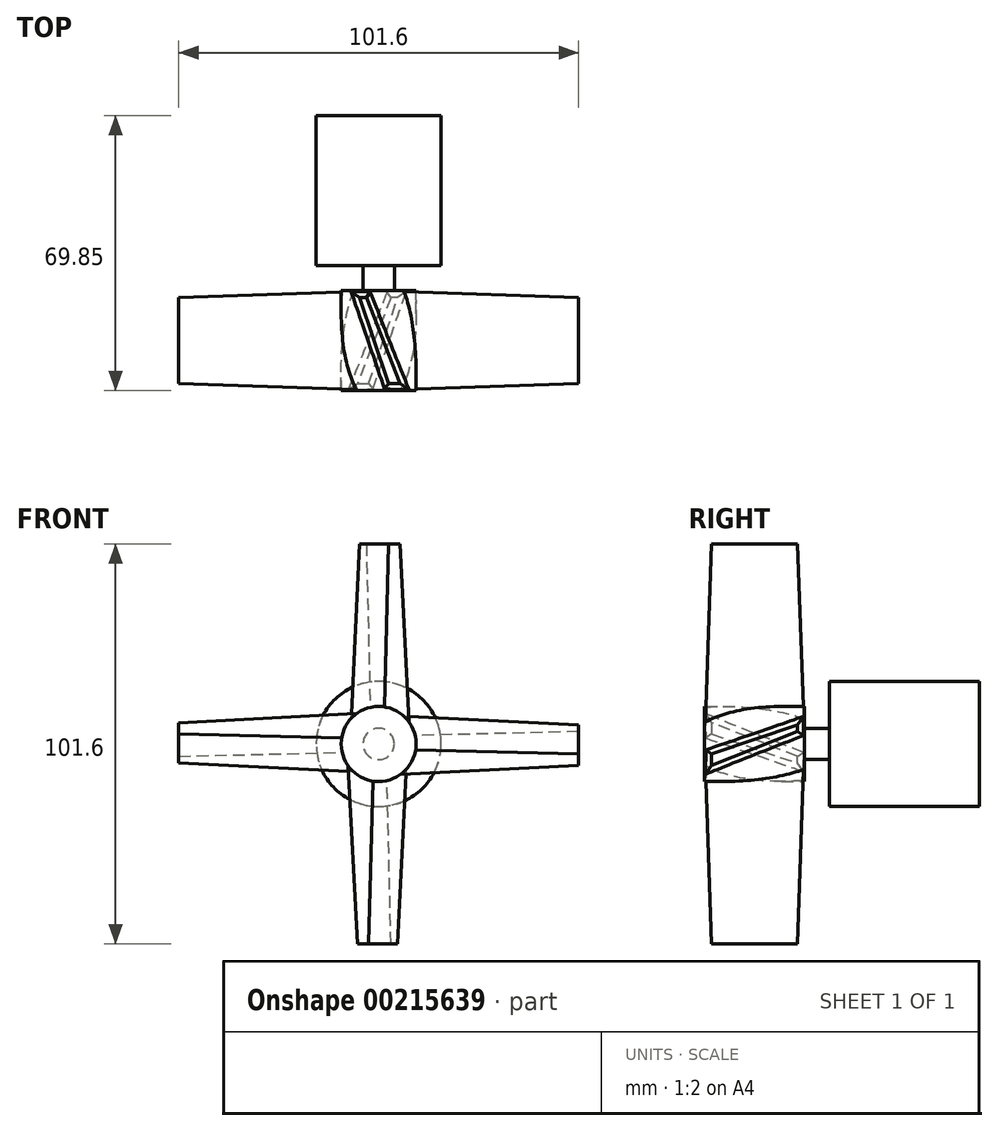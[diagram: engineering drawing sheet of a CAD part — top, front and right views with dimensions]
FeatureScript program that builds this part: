
annotation { "Feature Type Name" : "Feature", "Feature Type Description" : "" }
export const myFeature = defineFeature(function(context is Context, id is Id, definition is map)
    precondition{}
    {
        {
            var Q0;
            Q0=qCreatedBy(makeId("Front.planeOp"),FACE);
            var sketch = newSketch(context, id + "F0", { "sketchPlane" : qUnion([Q0])});
            skCircle(sketch, "E0", {"center": v(0, 0) * mm, "radius": 9.53 * mm});
            skSolve(sketch);
        }
        {
            var Q0;
            Q0=makeQuery(id+"F0.imprint","IMPRINT",FACE,{"disambiguationData":[TD([[makeQuery(id+"F0.imprint","IMPRINT",EDGE,{"derivedFrom":sQuery(id+"F0.wireOp",EDGE,"E0")}),1.0]])]});
            extrude(context, id + "F1", {"entities" : qUnion([Q0]), "depth" : 25.4 * mm});
        }
        {
            var Q0;
            Q0=qCreatedBy(makeId("Right.planeOp"),FACE);
            var sketch = newSketch(context, id + "F2", { "sketchPlane" : qUnion([Q0])});
            skLineSegment(sketch, "E1", {"start": v(0, 4.62) * mm, "end": v(-25.4, -4.62) * mm, "construction": true});
            skLineSegment(sketch, "E2", {"start": v(-12.7, 0) * mm, "end": v(0, 0) * mm, "construction": true});
            skPoint(sketch, "E3.orphan", {"position": v(-25.4, 0) * mm});
            skLineSegment(sketch, "E4", {"start": v(-12.7, 0) * mm, "end": v(-25.4, 0) * mm, "construction": true});
            skLineSegment(sketch, "E5", {"start": v(0, 7.33) * mm, "end": v(-25.4, -1.24) * mm});
            skLineSegment(sketch, "E6", {"start": v(0, 1.92) * mm, "end": v(-25.4, -8) * mm});
            skLineSegment(sketch, "E7", {"start": v(-25.4, -1.24) * mm, "end": v(-25.4, -8) * mm});
            skLineSegment(sketch, "E8", {"start": v(0, 7.33) * mm, "end": v(0, 1.92) * mm});
            skSolve(sketch);
        }
        {
            var Q0;
            Q0 = qSketchRegion(id + "F2", true);
            extrude(context, id + "F3", {"entities" : qUnion([Q0]), "depth" : 50.8 * mm, "hasDraft" : true, "draftAngle" : 2 * degree, "draftPullDirection" : true});
        }
        {
            var Q0;
            Q0=qCreatedBy(makeId("Right.planeOp"),FACE);
            var sketch = newSketch(context, id + "F4", { "sketchPlane" : qUnion([Q0])});
            skLineSegment(sketch, "E9", {"start": v(-25.4, 0) * mm, "end": v(0, 0) * mm});
            skSolve(sketch);
        }
        {
            var Q0;
            Q0=makeQuery(id+"F3.opExtrude","SWEPT_BODY",BODY,{"disambiguationData":[OSD([sQuery(id+"F2.wireOp",EDGE,"E5"),sQuery(id+"F2.wireOp",EDGE,"E6"),sQuery(id+"F2.wireOp",EDGE,"E7"),sQuery(id+"F2.wireOp",EDGE,"E8")])]});
            var Q1;
            Q1=sQuery(id+"F4.wireOp",EDGE,"E9");
            circularPattern(context, id + "F5", {"operationType" : NewBodyOperationType.ADD, "entities" : qUnion([Q0]), "axis" : qUnion([Q1]), "angle" : 360 * degree, "instanceCount" : 4, "equalSpace" : true});
        }
        {
            var Q0;
            Q0=makeQuery(id+"F1.opExtrude","CAP_FACE",FACE,{"disambiguationData":[OSD([sQuery(id+"F0.wireOp",EDGE,"E0")])],"isStart":true});
            var sketch = newSketch(context, id + "F6", { "sketchPlane" : qUnion([Q0])});
            skCircle(sketch, "E10", {"center": v(0, 0) * mm, "radius": 3.97 * mm});
            skSolve(sketch);
        }
        {
            var Q0;
            Q0 = qSketchRegion(id + "F6", true);
            extrude(context, id + "F7", {"entities" : qUnion([Q0]), "operationType" : NewBodyOperationType.ADD, "depth" : 6.35 * mm});
        }
        {
            var Q0;
            Q0=qCreatedBy(makeId("Right.planeOp"),FACE);
            var sketch = newSketch(context, id + "F8", { "sketchPlane" : qUnion([Q0])});
            skLineSegment(sketch, "E11.bottom", {"start": v(6.35, 15.88) * mm, "end": v(44.45, 15.88) * mm});
            skLineSegment(sketch, "E11.left", {"start": v(6.35, 15.88) * mm, "end": v(6.35, 0) * mm});
            skLineSegment(sketch, "E11.right", {"start": v(44.45, 15.88) * mm, "end": v(44.45, 0) * mm});
            skLineSegment(sketch, "E12", {"start": v(0, 0) * mm, "end": v(6.35, 0) * mm, "construction": true});
            skLineSegment(sketch, "E13", {"start": v(6.35, 0) * mm, "end": v(44.45, 0) * mm});
            skSolve(sketch);
        }
        {
            var Q0;
            Q0=makeQuery(id+"F8.imprint","IMPRINT",FACE,{"disambiguationData":[TD([[makeQuery(id+"F8.imprint","IMPRINT",EDGE,{"derivedFrom":sQuery(id+"F8.wireOp",EDGE,"E11.bottom")}),-1.0]])]});
            var Q1;
            Q1=sQuery(id+"F8.wireOp",EDGE,"E13");
            revolve(context, id + "F9", {"entities" : qUnion([Q0]), "axis" : qUnion([Q1]), "revolveType" : RevolveType.FULL});
        }
    });
